# Revit family: 306_64e1fcc9dcbd4348a09b226038a222
name_source: partatom
category: Pipe Accessories
units: mm (PartAtom-declared; Revit-internal decimal feet)

## family parameters
Always vertical = Yes
Cut with Voids When Loaded = No
Part Type = Valve - Breaks Into
Round Connector Dimension = Use Diameter
Shared = No
Work Plane-Based = No

## types (5) — shared parameters
B = 72 mm
CAT0 = Yes
Description = 3-way Change-over valve VRG232, PN10external thread
L2D_Min = 3048 mm
MC = No
Manufacturer = ESBE
QmdConnectorList = 301;D;302;D
URL = http://www.esbe.eu
X1 = 36 mm  [stored 0.11811 ft]
magiPartTypeId = 306
magiProductFamilyId = 64e1fcc9dcbd4348a09b226038a222

## per-type parameters (varying)
| type | A1 | AR | C | D | D1 | L2D | W2D | X2 | Y0 | Y00 | Y2 | Y3 | Y6 | Y7 | Y9 | Z5 | Z5__ve | magiProductId |
| VRG232 20-6.3 G 1 | 27 mm | 27 mm | 32 mm  [stored 0.104987 ft] | 20 mm | 50 mm  [stored 0.164042 ft] | 60 mm | 20 mm  [stored 0.0656168 ft] | 30 mm  [stored 0.0984252 ft] | 10 mm  [stored 0.0328084 ft] | 10 mm  [stored 0.0328084 ft] | 11 mm | 21 mm  [stored 0.0688976 ft] | 20 mm  [stored 0.0656168 ft] | 18 mm | 17 mm | 9 mm  [stored 0.0295276 ft] | -9 mm | 800b3706484847169f6b160795ef05 |
| VRG232 50-40 G 2¼ | 46 mm  [stored 0.150919 ft] | 46 mm  [stored 0.150919 ft] | 46 mm  [stored 0.150919 ft] | 50 mm | 64 mm | 108 mm | 50 mm  [stored 0.164042 ft] | 54 mm  [stored 0.177165 ft] | 26 mm | 25 mm  [stored 0.082021 ft] | 26 mm | 39 mm  [stored 0.127953 ft] | 38 mm  [stored 0.124672 ft] | 36 mm  [stored 0.11811 ft] | 35 mm  [stored 0.114829 ft] | 14 mm  [stored 0.0459318 ft] | -14 mm | 40fde46207d246148f8c1300991e73 |
| VRG232 40-30 G 2 | 40 mm  [stored 0.131234 ft] | 40 mm  [stored 0.131234 ft] | 44 mm  [stored 0.144357 ft] | 40 mm | 60 mm | 94 mm | 40 mm  [stored 0.131234 ft] | 47 mm  [stored 0.154199 ft] | 20 mm  [stored 0.0656168 ft] | 20 mm  [stored 0.0656168 ft] | 21 mm  [stored 0.0688976 ft] | 34 mm  [stored 0.111549 ft] | 33 mm | 31 mm | 30 mm  [stored 0.0984252 ft] | 13 mm | -13 mm | 07175bb08a544345915d8d5492e4c9 |
| VRG232 32-16 G 1½ | 36 mm  [stored 0.11811 ft] | 36 mm  [stored 0.11811 ft] | 37 mm  [stored 0.121391 ft] | 32 mm | 55 mm | 82 mm | 32 mm  [stored 0.104987 ft] | 41 mm  [stored 0.134514 ft] | 16 mm  [stored 0.0524934 ft] | 16 mm  [stored 0.0524934 ft] | 17 mm | 29 mm | 28 mm | 27 mm | 26 mm | 11 mm | -11 mm | fcffcb4879654915a2759acbfb336f |
| VRG232 25-10 G 1¼ | 31 mm | 31 mm | 34 mm  [stored 0.111549 ft] | 25 mm | 52 mm  [stored 0.170604 ft] | 70 mm | 25 mm  [stored 0.082021 ft] | 35 mm  [stored 0.114829 ft] | 13 mm | 13 mm | 13 mm | 25 mm  [stored 0.082021 ft] | 24 mm | 22 mm | 21 mm  [stored 0.0688976 ft] | 10 mm  [stored 0.0328084 ft] | -10 mm  [stored -0.0328084 ft] | 2ee924d9e4eb42528123301669c0f3 |

note: column(s) folded — value = type name in every type: magiProductCode

note: [stored X ft] marks values corroborated as IEEE doubles in the binary element streams (Revit-internal decimal feet)

## geometry (parser evidence)
native form markers: Sweep x1
no freeform markers — native parametric forms only
